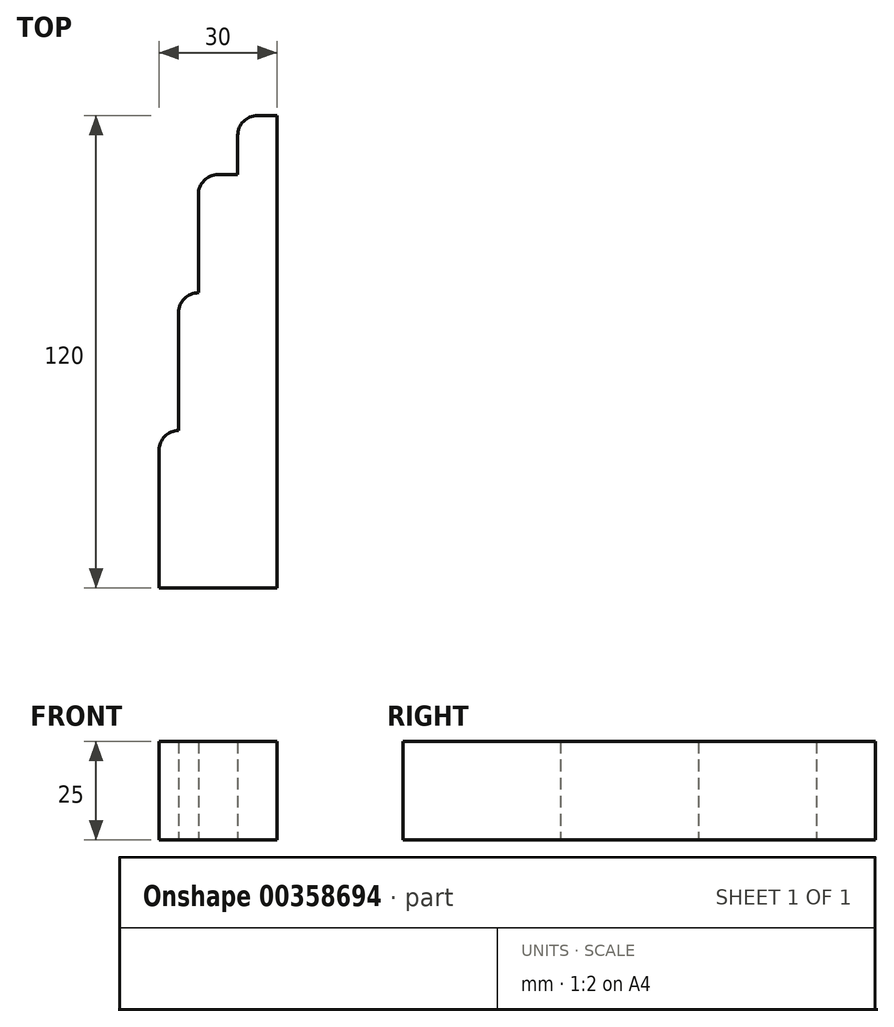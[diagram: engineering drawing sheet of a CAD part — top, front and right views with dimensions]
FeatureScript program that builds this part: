
annotation { "Feature Type Name" : "Feature", "Feature Type Description" : "" }
export const myFeature = defineFeature(function(context is Context, id is Id, definition is map)
    precondition{}
    {
        {
            var Q0;
            Q0=qCreatedBy(makeId("Top.planeOp"),FACE);
            var sketch = newSketch(context, id + "F0", { "sketchPlane" : qUnion([Q0])});
            skLineSegment(sketch, "E0", {"start": v(-65.86, -58.84) * mm, "end": v(-35.86, -58.84) * mm});
            skLineSegment(sketch, "E1", {"start": v(-35.86, -58.84) * mm, "end": v(-35.86, 61.16) * mm});
            skLineSegment(sketch, "E2", {"start": v(-35.86, 61.16) * mm, "end": v(-45.86, 61.16) * mm});
            skLineSegment(sketch, "E3", {"start": v(-45.86, 61.16) * mm, "end": v(-45.86, 46.16) * mm});
            skLineSegment(sketch, "E4", {"start": v(-45.86, 46.16) * mm, "end": v(-55.86, 46.16) * mm});
            skLineSegment(sketch, "E5", {"start": v(-55.86, 46.16) * mm, "end": v(-55.86, 16.16) * mm});
            skLineSegment(sketch, "E6", {"start": v(-55.86, 16.16) * mm, "end": v(-60.86, 16.16) * mm});
            skLineSegment(sketch, "E7", {"start": v(-60.86, 16.16) * mm, "end": v(-60.86, -18.84) * mm});
            skLineSegment(sketch, "E8", {"start": v(-60.86, -18.84) * mm, "end": v(-65.86, -18.84) * mm});
            skLineSegment(sketch, "E9", {"start": v(-65.86, -18.84) * mm, "end": v(-65.86, -58.84) * mm});
            skLineSegment(sketch, "E10", {"start": v(25, -58.84) * mm, "end": v(25, 61.16) * mm});
            skLineSegment(sketch, "E11", {"start": v(25, 61.16) * mm, "end": v(20, 61.16) * mm});
            skLineSegment(sketch, "E12", {"start": v(15, 56.16) * mm, "end": v(15, 46.16) * mm});
            skLineSegment(sketch, "E13", {"start": v(15, 46.16) * mm, "end": v(10, 46.16) * mm});
            skLineSegment(sketch, "E14", {"start": v(5, 41.16) * mm, "end": v(5, 16.16) * mm});
            skLineSegment(sketch, "E15", {"start": v(5, 16.16) * mm, "end": v(5, 16.16) * mm});
            skLineSegment(sketch, "E16", {"start": v(0, 11.16) * mm, "end": v(0, -18.84) * mm});
            skLineSegment(sketch, "E17", {"start": v(0, -18.84) * mm, "end": v(0, -18.84) * mm});
            skLineSegment(sketch, "E18", {"start": v(-5, -23.84) * mm, "end": v(-5, -58.84) * mm});
            skLineSegment(sketch, "E19", {"start": v(-5, -58.84) * mm, "end": v(25, -58.84) * mm});
            skPoint(sketch, "E20.visualSharp", {"position": v(-5, -18.84) * mm});
            skArc(sketch, "E20.filletArc", {"start": v(0, -18.84) * mm, "mid": v(-3.54, -20.3) * mm, "end": v(-5, -23.84) * mm});
            skPoint(sketch, "E21.visualSharp", {"position": v(0, 16.16) * mm});
            skArc(sketch, "E21.filletArc", {"start": v(5, 16.16) * mm, "mid": v(1.46, 14.7) * mm, "end": v(0, 11.16) * mm});
            skPoint(sketch, "E22.visualSharp", {"position": v(5, 46.16) * mm});
            skArc(sketch, "E22.filletArc", {"start": v(10, 46.16) * mm, "mid": v(6.46, 44.7) * mm, "end": v(5, 41.16) * mm});
            skPoint(sketch, "E23.visualSharp", {"position": v(15, 61.16) * mm});
            skArc(sketch, "E23.filletArc", {"start": v(20, 61.16) * mm, "mid": v(16.46, 59.7) * mm, "end": v(15, 56.16) * mm});
            skSolve(sketch);
        }
        {
            var Q0;
            Q0=makeQuery(id+"F0.imprint","IMPRINT",FACE,{"disambiguationData":[TD([[makeQuery(id+"F0.imprint","IMPRINT",EDGE,{"derivedFrom":sQuery(id+"F0.wireOp",EDGE,"E10")}),1.0]])]});
            extrude(context, id + "F1", {"entities" : qUnion([Q0]), "depth" : 25 * mm});
        }
    });
